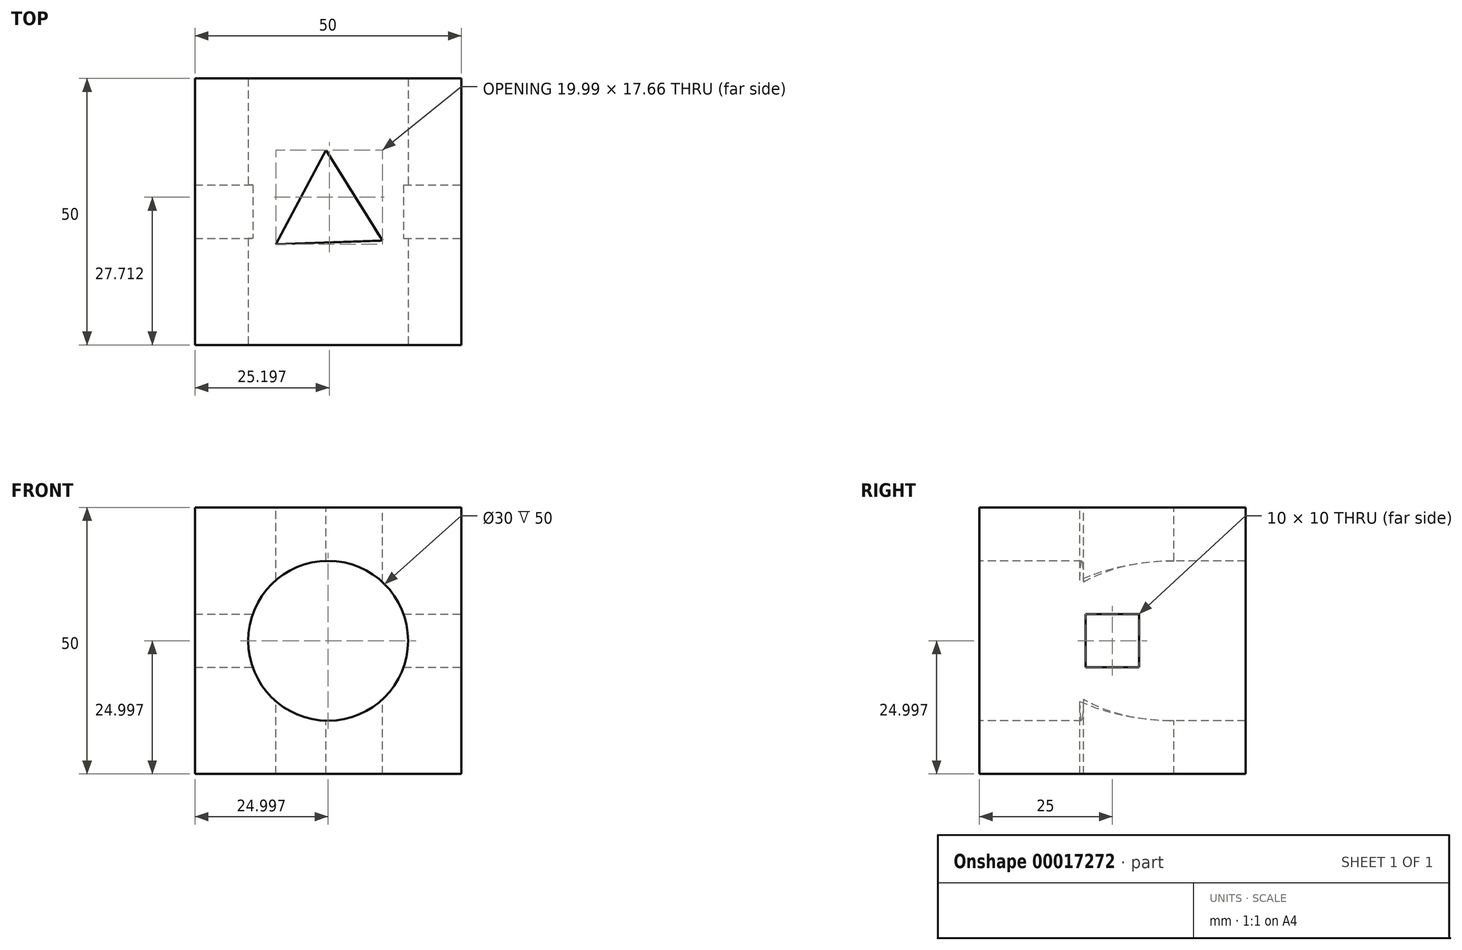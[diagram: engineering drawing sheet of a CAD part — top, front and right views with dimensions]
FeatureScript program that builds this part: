
annotation { "Feature Type Name" : "Feature", "Feature Type Description" : "" }
export const myFeature = defineFeature(function(context is Context, id is Id, definition is map)
    precondition{}
    {
        {
            var Q0;
            Q0=qCreatedBy(makeId("Front.planeOp"),FACE);
            var sketch = newSketch(context, id + "F0", { "sketchPlane" : qUnion([Q0])});
            skLineSegment(sketch, "E0", {"start": v(-15.96, 31.24) * mm, "end": v(-15.96, -18.76) * mm});
            skLineSegment(sketch, "E1", {"start": v(-15.96, -18.76) * mm, "end": v(34.04, -18.76) * mm});
            skLineSegment(sketch, "E2", {"start": v(34.04, -18.76) * mm, "end": v(34.04, 31.24) * mm});
            skLineSegment(sketch, "E3", {"start": v(34.04, 31.24) * mm, "end": v(-15.96, 31.24) * mm});
            skSolve(sketch);
        }
        {
            var Q0;
            Q0 = qSketchRegion(id + "F0", true);
            extrude(context, id + "F1", {"entities" : qUnion([Q0]), "depth" : 50 * mm});
        }
        {
            var Q0;
            Q0=makeQuery(id+"F1.opExtrude","CAP_FACE",FACE,{"disambiguationData":[OSD([sQuery(id+"F0.wireOp",EDGE,"E0"),sQuery(id+"F0.wireOp",EDGE,"E1"),sQuery(id+"F0.wireOp",EDGE,"E2"),sQuery(id+"F0.wireOp",EDGE,"E3")])],"isStart":false});
            var sketch = newSketch(context, id + "F2", { "sketchPlane" : qUnion([Q0])});
            skCircle(sketch, "E4", {"center": v(9.04, 6.24) * mm, "radius": 15 * mm});
            skSolve(sketch);
        }
        {
            var Q0;
            Q0 = qSketchRegion(id + "F2", true);
            extrude(context, id + "F3", {"entities" : qUnion([Q0]), "operationType" : NewBodyOperationType.REMOVE, "endBound" : BoundingType.THROUGH_ALL, "oppositeDirection" : true, "depth" : 25 * mm});
        }
        {
            var Q0;
            Q0=makeQuery(id+"F1.opExtrude","SWEPT_FACE",FACE,{"disambiguationData":[OSD([sQuery(id+"F0.wireOp",EDGE,"E2")])]});
            var sketch = newSketch(context, id + "F4", { "sketchPlane" : qUnion([Q0])});
            skLineSegment(sketch, "E5.bottom", {"start": v(-25, 6.24) * mm, "end": v(-30, 6.24) * mm});
            skLineSegment(sketch, "E5.top", {"start": v(-25, 11.24) * mm, "end": v(-30, 11.24) * mm});
            skLineSegment(sketch, "E5.left", {"start": v(-25, 6.24) * mm, "end": v(-25, 11.24) * mm});
            skLineSegment(sketch, "E5.right", {"start": v(-30, 6.24) * mm, "end": v(-30, 11.24) * mm});
            skLineSegment(sketch, "E6.bottom", {"start": v(-25, 11.24) * mm, "end": v(-20, 11.24) * mm});
            skLineSegment(sketch, "E6.top", {"start": v(-25, 6.24) * mm, "end": v(-20, 6.24) * mm});
            skLineSegment(sketch, "E6.left", {"start": v(-25, 11.24) * mm, "end": v(-25, 6.24) * mm});
            skLineSegment(sketch, "E6.right", {"start": v(-20, 11.24) * mm, "end": v(-20, 6.24) * mm});
            skLineSegment(sketch, "E7.top", {"start": v(-25, 1.24) * mm, "end": v(-20, 1.24) * mm});
            skLineSegment(sketch, "E7.left", {"start": v(-25, 6.24) * mm, "end": v(-25, 1.24) * mm});
            skLineSegment(sketch, "E7.right", {"start": v(-20, 6.24) * mm, "end": v(-20, 1.24) * mm});
            skLineSegment(sketch, "E8.top", {"start": v(-25, 1.24) * mm, "end": v(-30, 1.24) * mm});
            skLineSegment(sketch, "E8.right", {"start": v(-30, 6.24) * mm, "end": v(-30, 1.24) * mm});
            skSolve(sketch);
        }
        {
            var Q0;
            Q0 = qSketchRegion(id + "F4", true);
            extrude(context, id + "F5", {"entities" : qUnion([Q0]), "operationType" : NewBodyOperationType.REMOVE, "endBound" : BoundingType.THROUGH_ALL, "oppositeDirection" : true, "depth" : 25 * mm});
        }
        {
            var Q0;
            Q0=makeQuery(id+"F1.opExtrude","SWEPT_FACE",FACE,{"disambiguationData":[OSD([sQuery(id+"F0.wireOp",EDGE,"E3")])]});
            var sketch = newSketch(context, id + "F6", { "sketchPlane" : qUnion([Q0])});
            skCircle(sketch, "E9.cCircle", {"center": v(9.04, -25) * mm, "radius": 5.77 * mm, "construction": true});
            skLineSegment(sketch, "E9.0", {"start": v(-0.76, -31.12) * mm, "end": v(8.64, -13.46) * mm});
            skLineSegment(sketch, "E9.1", {"start": v(8.64, -13.46) * mm, "end": v(19.23, -30.42) * mm});
            skLineSegment(sketch, "E9.2", {"start": v(19.23, -30.42) * mm, "end": v(-0.76, -31.12) * mm});
            skPoint(sketch, "E9.0.midPoint", {"position": v(3.94, -22.29) * mm});
            skSolve(sketch);
        }
        {
            var Q0;
            Q0 = qSketchRegion(id + "F6", true);
            extrude(context, id + "F7", {"entities" : qUnion([Q0]), "operationType" : NewBodyOperationType.REMOVE, "endBound" : BoundingType.THROUGH_ALL, "oppositeDirection" : true, "depth" : 25 * mm});
        }
    });
